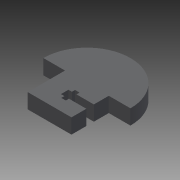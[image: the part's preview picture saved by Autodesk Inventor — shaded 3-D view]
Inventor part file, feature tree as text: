
AUTODESK INVENTOR PART (.ipt)
format: ipt  version: 2013 (Build 170138000, 138)  size: 98,816 bytes
history: native  units: mm
features: extrude x1, sketch x1
ambient origin geometry x8: Origin, YZ Plane, XZ Plane, XY Plane, X Axis, Y Axis, Z Axis, Center Point
bodies: Solid1 (feature_tree)
feature tree (2):
  extrude  "Extrusion1"  [1 undecoded]
  sketch  "Sketch1"  dims[d0=6.0mm d1=0.0mm]
note: 1 required parameter value undecoded (feature->parameter linkage not recoverable at this tier; creation-order binding heuristic only, values carry confidence <= 0.55)
